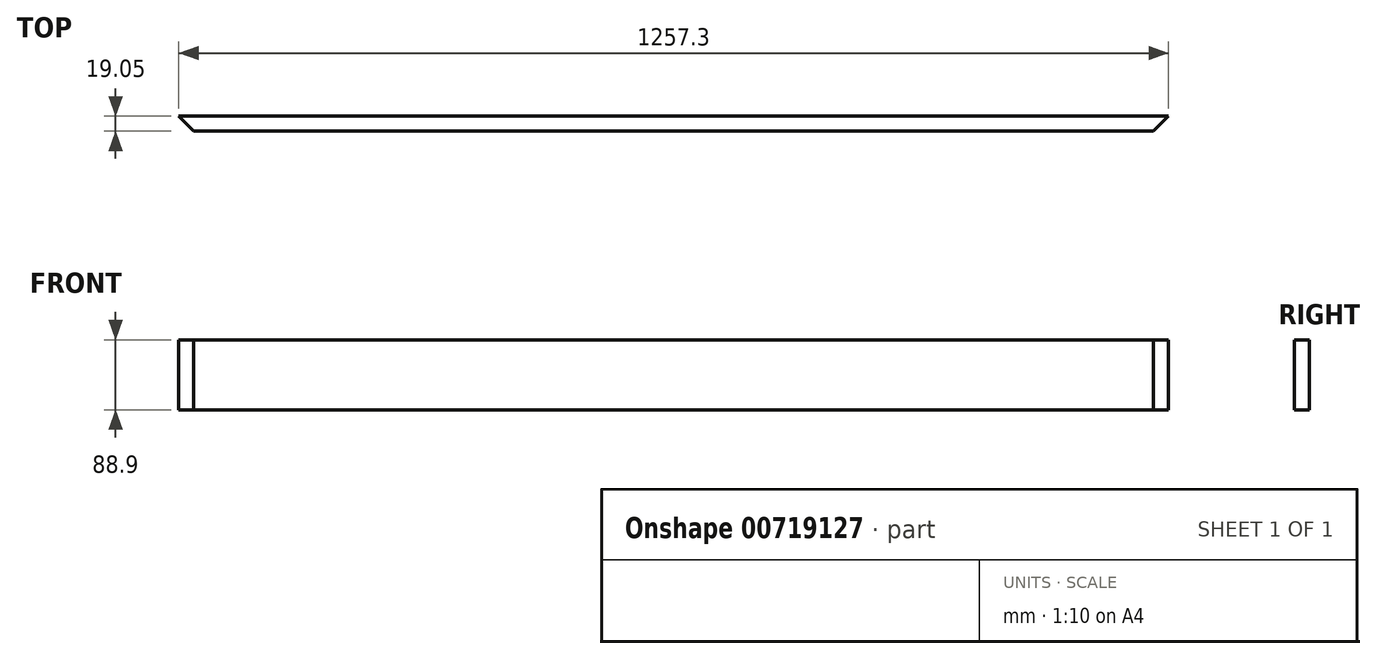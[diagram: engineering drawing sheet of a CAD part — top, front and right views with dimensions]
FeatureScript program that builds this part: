
annotation { "Feature Type Name" : "Feature", "Feature Type Description" : "" }
export const myFeature = defineFeature(function(context is Context, id is Id, definition is map)
    precondition{}
    {
        {
            var Q0;
            Q0=qCreatedBy(makeId("Front.planeOp"),FACE);
            var sketch = newSketch(context, id + "F0", { "sketchPlane" : qUnion([Q0])});
            skLineSegment(sketch, "E0.bottom", {"start": v(0, 0) * mm, "end": v(-1257.3, 0) * mm});
            skLineSegment(sketch, "E0.top", {"start": v(0, 88.9) * mm, "end": v(-1257.3, 88.9) * mm});
            skLineSegment(sketch, "E0.left", {"start": v(0, 0) * mm, "end": v(0, 88.9) * mm});
            skLineSegment(sketch, "E0.right", {"start": v(-1257.3, 0) * mm, "end": v(-1257.3, 88.9) * mm});
            skSolve(sketch);
        }
        {
            var Q0;
            Q0 = qSketchRegion(id + "F0", true);
            extrude(context, id + "F1", {"entities" : qUnion([Q0]), "depth" : 19.05 * mm, "offsetDistance" : 25.4 * mm});
        }
        {
            var Q0;
            Q0=makeQuery(id+"F1.opExtrude","SWEPT_FACE",FACE,{"disambiguationData":[OSD([sQuery(id+"F0.wireOp",EDGE,"E0.bottom")])]});
            var sketch = newSketch(context, id + "F2", { "sketchPlane" : qUnion([Q0])});
            skLineSegment(sketch, "E1", {"start": v(-1257.3, 0) * mm, "end": v(-1238.25, 19.05) * mm});
            skLineSegment(sketch, "E2", {"start": v(-1238.25, 19.05) * mm, "end": v(-1257.3, 19.05) * mm});
            skLineSegment(sketch, "E3", {"start": v(-1257.3, 19.05) * mm, "end": v(-1257.3, 0) * mm});
            skSolve(sketch);
        }
        {
            var Q0;
            Q0 = qSketchRegion(id + "F2", true);
            extrude(context, id + "F3", {"entities" : qUnion([Q0]), "operationType" : NewBodyOperationType.REMOVE, "oppositeDirection" : true, "depth" : 127 * mm, "offsetDistance" : 25.4 * mm});
        }
        {
            var Q0;
            Q0=makeQuery(id+"F1.opExtrude","SWEPT_FACE",FACE,{"disambiguationData":[OSD([sQuery(id+"F0.wireOp",EDGE,"E0.bottom")])]});
            var sketch = newSketch(context, id + "F4", { "sketchPlane" : qUnion([Q0])});
            skLineSegment(sketch, "E4", {"start": v(0, 0) * mm, "end": v(-19.05, 19.05) * mm});
            skLineSegment(sketch, "E5", {"start": v(-19.05, 19.05) * mm, "end": v(0, 19.05) * mm});
            skLineSegment(sketch, "E6", {"start": v(0, 19.05) * mm, "end": v(0, 0) * mm});
            skSolve(sketch);
        }
        {
            var Q0;
            Q0 = qSketchRegion(id + "F4", true);
            extrude(context, id + "F5", {"entities" : qUnion([Q0]), "operationType" : NewBodyOperationType.REMOVE, "oppositeDirection" : true, "depth" : 127 * mm, "offsetDistance" : 25.4 * mm});
        }
    });
